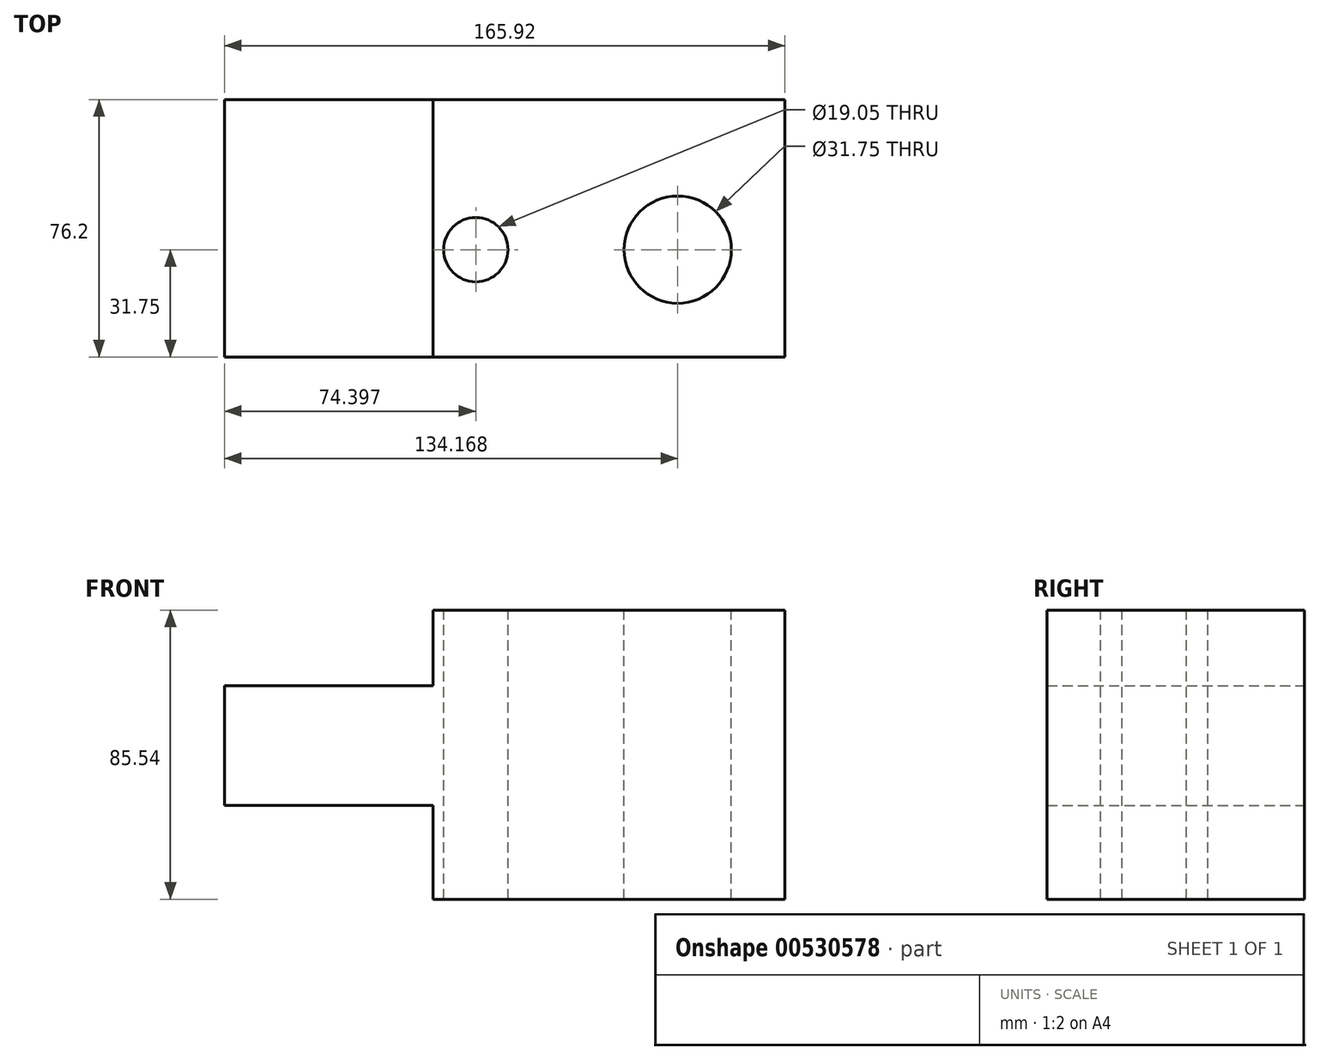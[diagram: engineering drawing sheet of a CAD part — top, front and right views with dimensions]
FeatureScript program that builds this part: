
annotation { "Feature Type Name" : "Feature", "Feature Type Description" : "" }
export const myFeature = defineFeature(function(context is Context, id is Id, definition is map)
    precondition{}
    {
        {
            var Q0;
            Q0=qCreatedBy(makeId("Front.planeOp"),FACE);
            var sketch = newSketch(context, id + "F0", { "sketchPlane" : qUnion([Q0])});
            skLineSegment(sketch, "E0.bottom", {"start": v(-43.75, 42.9) * mm, "end": v(60.47, 42.9) * mm});
            skLineSegment(sketch, "E0.top", {"start": v(-43.75, -42.65) * mm, "end": v(60.47, -42.65) * mm});
            skLineSegment(sketch, "E0.left", {"start": v(-43.75, 42.9) * mm, "end": v(-43.75, 20.52) * mm});
            skLineSegment(sketch, "E0.right", {"start": v(60.47, 42.9) * mm, "end": v(60.47, -42.65) * mm});
            skLineSegment(sketch, "E1.bottom", {"start": v(-105.45, 20.52) * mm, "end": v(-43.75, 20.52) * mm});
            skLineSegment(sketch, "E1.top", {"start": v(-105.45, -14.87) * mm, "end": v(-43.75, -14.87) * mm});
            skLineSegment(sketch, "E1.left", {"start": v(-105.45, 20.52) * mm, "end": v(-105.45, -14.87) * mm});
            skLineSegment(sketch, "E2.trimOffspring", {"start": v(-43.75, -14.87) * mm, "end": v(-43.75, -42.65) * mm});
            skSolve(sketch);
        }
        {
            var Q0;
            Q0=makeQuery(id+"F0.imprint","IMPRINT",FACE,{"disambiguationData":[TD([[makeQuery(id+"F0.imprint","IMPRINT",EDGE,{"derivedFrom":sQuery(id+"F0.wireOp",EDGE,"E1.bottom")}),-1.0]])]});
            var Q1;
            {var subQ3=sQuery(id+"F0.wireOp",EDGE,"E0.bottom");Q1=makeQuery(id+"F0.imprint","IMPRINT",FACE,{"disambiguationData":[TD([[makeQuery(id+"F0.imprint","IMPRINT",EDGE,{"derivedFrom":subQ3}),-1.0]])]});}
            var Q2;
            Q2=sQuery(id+"F0.wireOp",EDGE,"E1.bottom");
            var Q3;
            Q3=sQuery(id+"F0.wireOp",EDGE,"E1.left");
            var Q4;
            Q4=sQuery(id+"F0.wireOp",EDGE,"E1.top");
            var Q5;
            Q5=sQuery(id+"F0.wireOp",EDGE,"E0.left");
            extrude(context, id + "F1", {"entities" : qUnion([Q0, Q1]), "surfaceEntities" : qUnion([Q2, Q3, Q4, Q5]), "depth" : 76.2 * mm, "offsetDistance" : 25.4 * mm});
        }
        {
            var Q0;
            Q0=makeQuery(id+"F1.opExtrude","SWEPT_FACE",FACE,{"disambiguationData":[OSD([sQuery(id+"F0.wireOp",EDGE,"E0.bottom")])]});
            var sketch = newSketch(context, id + "F2", { "sketchPlane" : qUnion([Q0])});
            skCircle(sketch, "E3", {"center": v(28.72, -44.45) * mm, "radius": 15.88 * mm});
            skCircle(sketch, "E4", {"center": v(-31.05, -44.45) * mm, "radius": 9.53 * mm});
            skSolve(sketch);
        }
        {
            var Q0;
            Q0 = qSketchRegion(id + "F2", true);
            extrude(context, id + "F3", {"entities" : qUnion([Q0]), "operationType" : NewBodyOperationType.REMOVE, "endBound" : BoundingType.UP_TO_NEXT, "oppositeDirection" : true, "depth" : 25.4 * mm, "offsetDistance" : 25.4 * mm});
        }
    });
